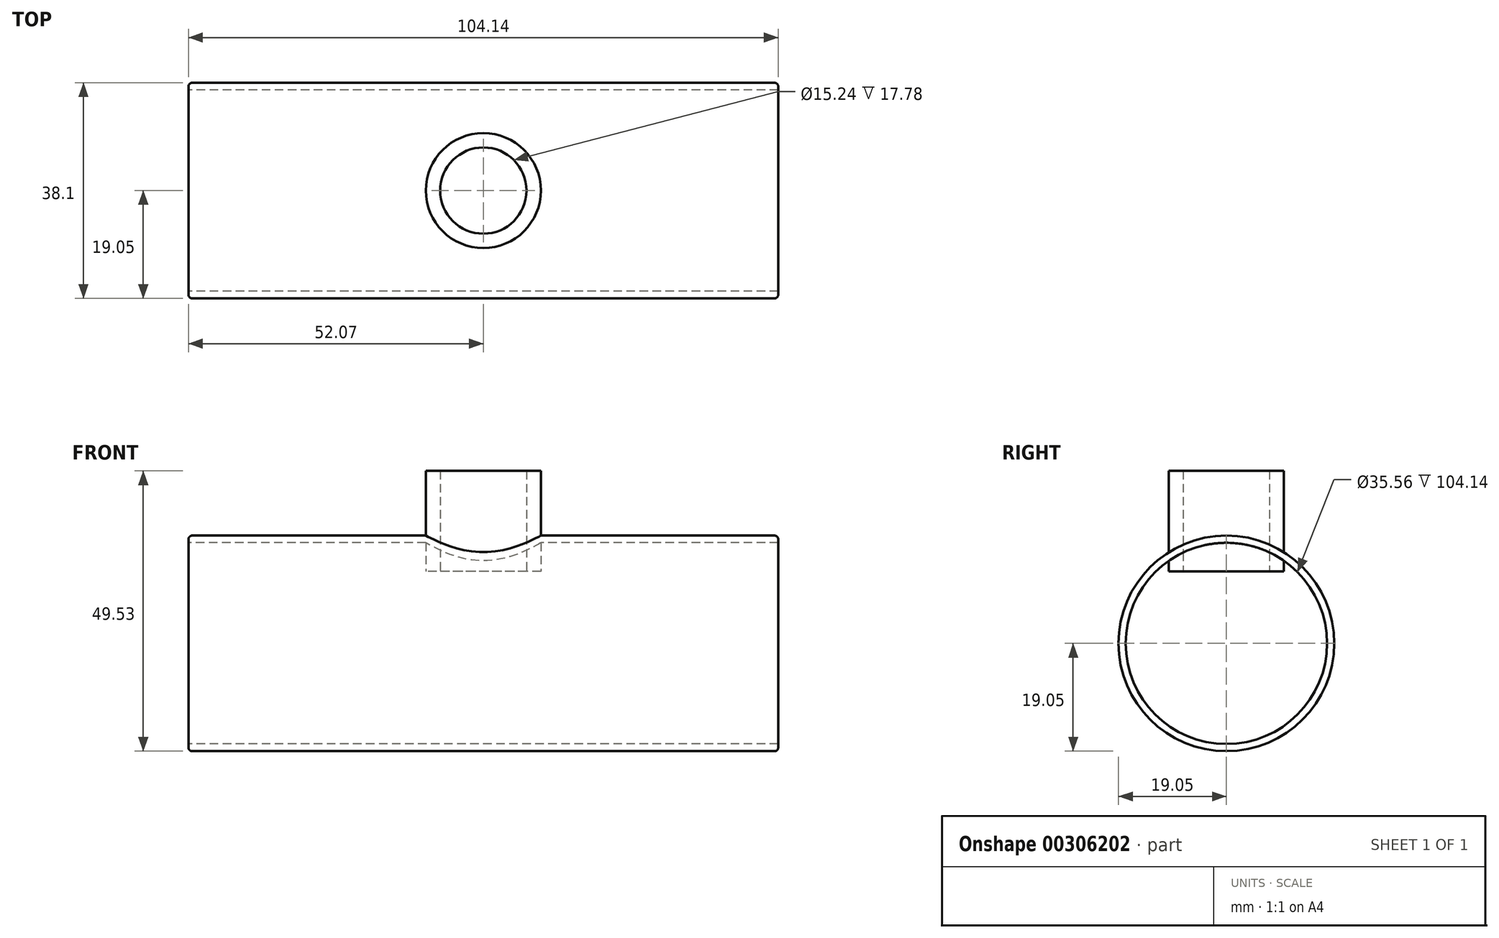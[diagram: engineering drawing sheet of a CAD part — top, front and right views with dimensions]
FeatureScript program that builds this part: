
annotation { "Feature Type Name" : "Feature", "Feature Type Description" : "" }
export const myFeature = defineFeature(function(context is Context, id is Id, definition is map)
    precondition{}
    {
        {
            var Q0;
            Q0=qCreatedBy(makeId("Right.planeOp"),FACE);
            var sketch = newSketch(context, id + "F0", { "sketchPlane" : qUnion([Q0])});
            skCircle(sketch, "E0", {"center": v(0, 0) * mm, "radius": 17.78 * mm});
            skCircle(sketch, "E1", {"center": v(0, 0) * mm, "radius": 19.05 * mm});
            skSolve(sketch);
        }
        {
            var Q0;
            Q0=qSketchRegion(id+"F0",true);
            extrude(context, id + "F1", {"entities" : qUnion([Q0]), "depth" : 104.14 * mm, "symmetric" : true});
        }
        {
            var Q0;
            Q0=makeQuery(id+"F1.opExtrude","CAP_EDGE",EDGE,{"disambiguationData":[OSD([sQuery(id+"F0.wireOp",EDGE,"E1")])],"isStart":false});
            var Q1;
            Q1=makeQuery(id+"F1.opExtrude","CAP_EDGE",EDGE,{"disambiguationData":[OSD([sQuery(id+"F0.wireOp",EDGE,"E1")])],"isStart":true});
            fillet(context, id + "F2", {"entities" : qUnion([Q0, Q1]), "radius" : 0.64 * mm, "tangentPropagation" : true, "allowEdgeOverflow" : false});
        }
        {
            var Q0;
            Q0=qCreatedBy(makeId("Top.planeOp"),FACE);
            var sketch = newSketch(context, id + "F3", { "sketchPlane" : qUnion([Q0])});
            skCircle(sketch, "E2", {"center": v(0, 0) * mm, "radius": 10.16 * mm});
            skCircle(sketch, "E3", {"center": v(0, 0) * mm, "radius": 7.62 * mm});
            skSolve(sketch);
        }
        {
            var Q0;
            Q0=qSketchRegion(id+"F3",true);
            extrude(context, id + "F4", {"entities" : qUnion([Q0]), "operationType" : NewBodyOperationType.ADD, "depth" : 30.48 * mm});
        }
        {
            var Q0;
            Q0=qCreatedBy(makeId("Top.planeOp"),FACE);
            var sketch = newSketch(context, id + "F5", { "sketchPlane" : qUnion([Q0])});
            skCircle(sketch, "E4", {"center": v(0, 0) * mm, "radius": 7.62 * mm});
            skSolve(sketch);
        }
        {
            var Q0;
            Q0=qSketchRegion(id+"F5",true);
            extrude(context, id + "F6", {"entities" : qUnion([Q0]), "operationType" : NewBodyOperationType.REMOVE, "endBound" : BoundingType.THROUGH_ALL, "depth" : 5.08 * mm});
        }
        {
            var Q0;
            Q0=qCreatedBy(makeId("Right.planeOp"),FACE);
            var sketch = newSketch(context, id + "F7", { "sketchPlane" : qUnion([Q0])});
            skArc(sketch, "E5", {"start": v(-10.16, 14.6) * mm, "mid": v(0, -17.78) * mm, "end": v(10.16, 14.6) * mm});
            skLineSegment(sketch, "E6", {"start": v(-10.16, 12.7) * mm, "end": v(10.16, 12.7) * mm});
            skLineSegment(sketch, "E7", {"start": v(-10.16, 14.6) * mm, "end": v(-10.16, 12.7) * mm});
            skLineSegment(sketch, "E8", {"start": v(10.16, 12.7) * mm, "end": v(10.16, 14.6) * mm});
            skPoint(sketch, "E9.MirrorCS.end.orphan", {"position": v(10.16, 0) * mm});
            skSolve(sketch);
        }
        {
            var Q0;
            Q0=qSketchRegion(id+"F7",true);
            extrude(context, id + "F8", {"entities" : qUnion([Q0]), "operationType" : NewBodyOperationType.REMOVE, "depth" : 50.8 * mm, "symmetric" : true});
        }
    });
